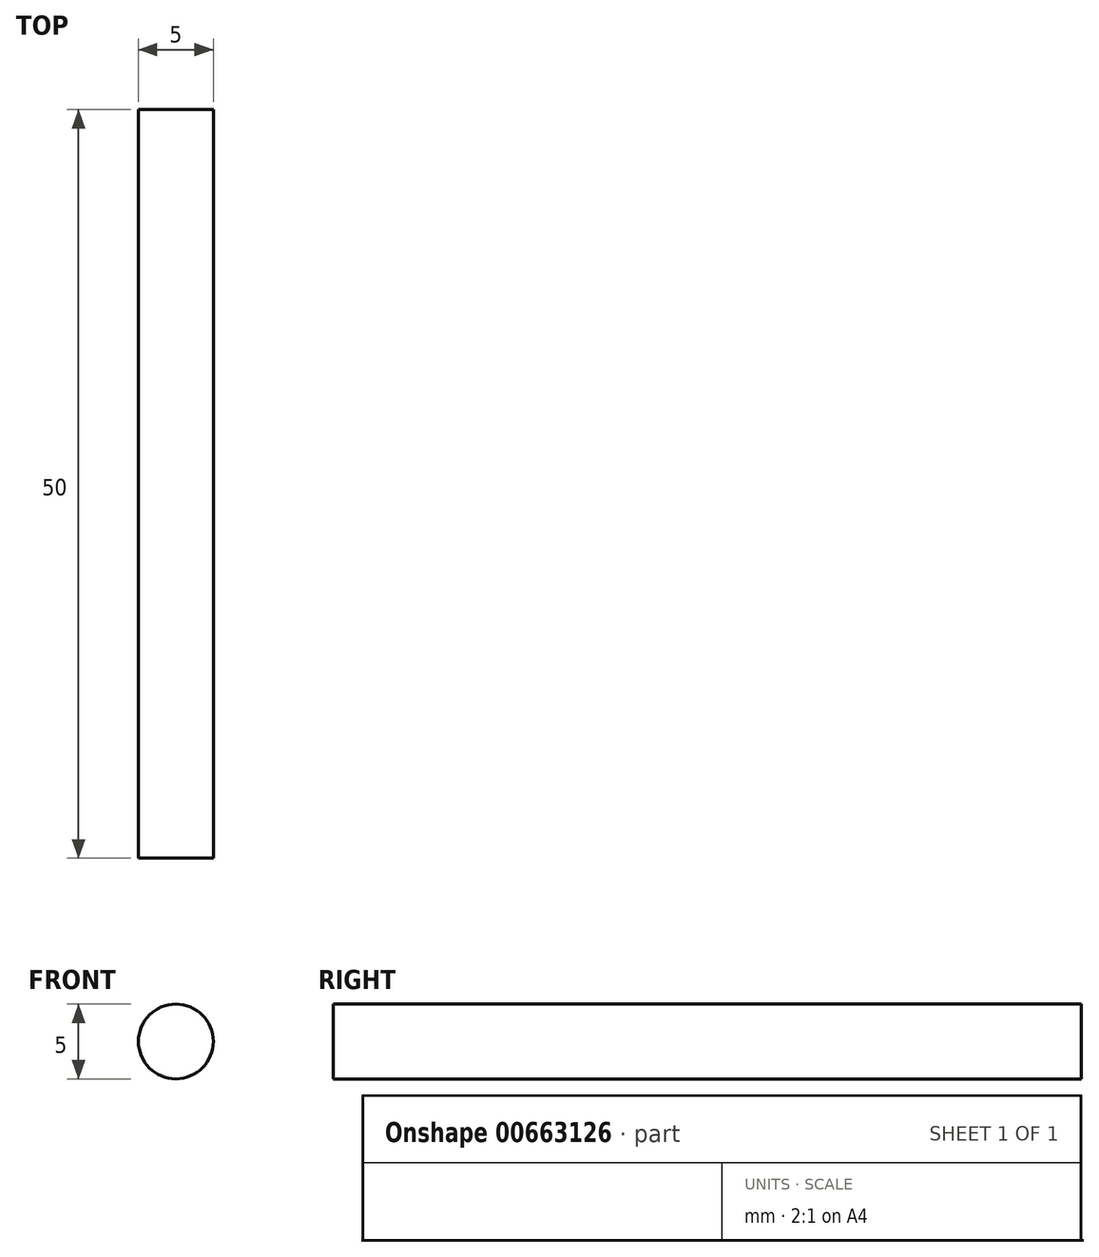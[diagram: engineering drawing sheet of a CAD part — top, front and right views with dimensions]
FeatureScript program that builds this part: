
annotation { "Feature Type Name" : "Feature", "Feature Type Description" : "" }
export const myFeature = defineFeature(function(context is Context, id is Id, definition is map)
    precondition{}
    {
        {
            var Q0;
            Q0=qCreatedBy(makeId("Front.planeOp"),FACE);
            var sketch = newSketch(context, id + "F0", { "sketchPlane" : qUnion([Q0])});
            skCircle(sketch, "E0", {"center": v(0, 0) * mm, "radius": 2.5 * mm});
            skSolve(sketch);
        }
        {
            var Q0;
            Q0=makeQuery(id+"F0.imprint","IMPRINT",FACE,{"disambiguationData":[TD([[makeQuery(id+"F0.imprint","IMPRINT",EDGE,{"derivedFrom":sQuery(id+"F0.wireOp",EDGE,"E0")}),1.0]])]});
            extrude(context, id + "F1", {"entities" : qUnion([Q0]), "oppositeDirection" : true, "depth" : 50 * mm, "offsetDistance" : 25 * mm});
        }
    });
